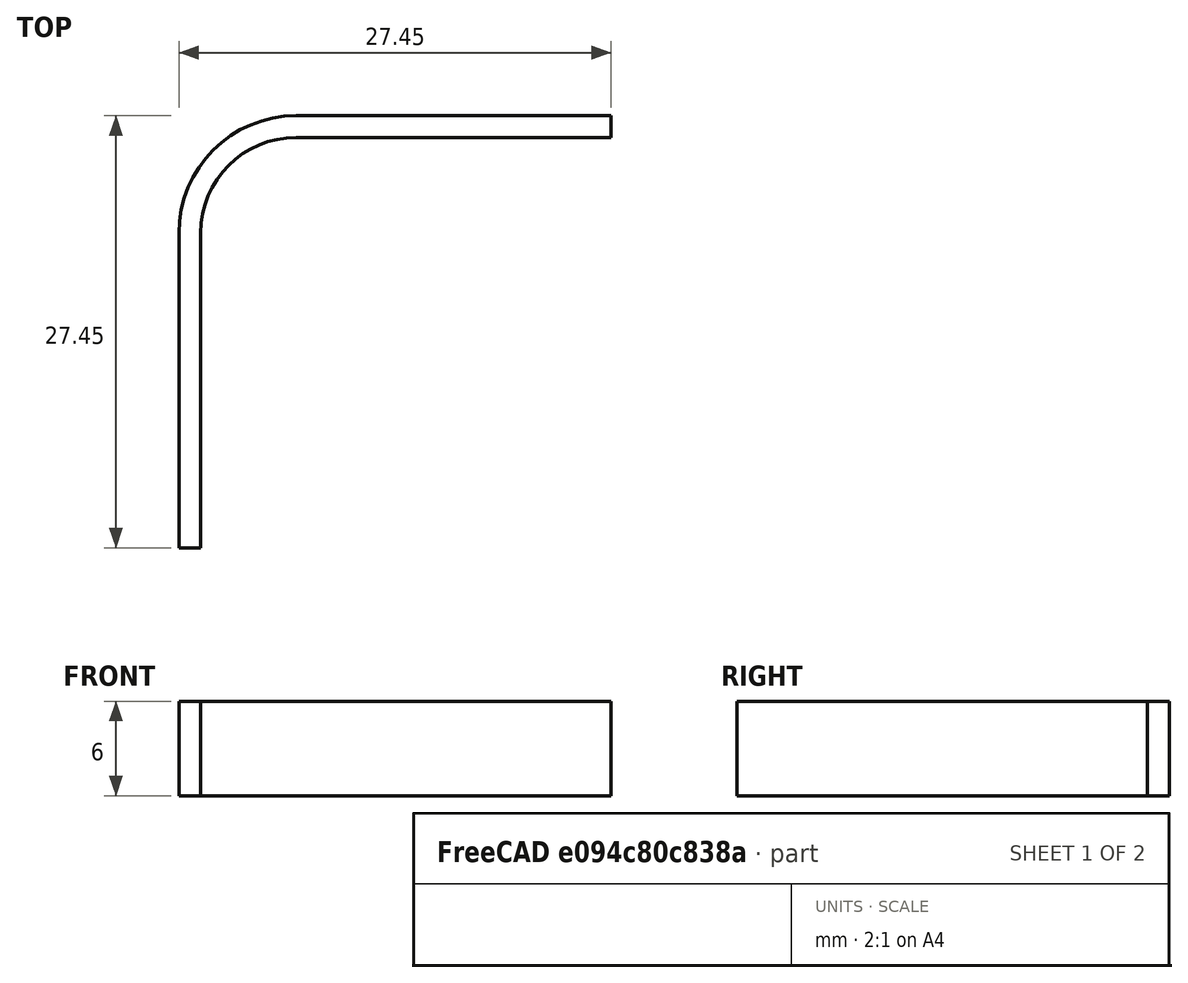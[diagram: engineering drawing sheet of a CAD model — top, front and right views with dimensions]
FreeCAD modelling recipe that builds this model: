
FCSTD DOCUMENT  (FreeCAD 0.20R27078 (Git))
Label: belt 20 idler 90 deg
License: All rights reserved
LicenseURL: http://en.wikipedia.org/wiki/All_rights_reserved
objects: Sketcher::SketchObject×2, PartDesign::AdditivePipe×1, PartDesign::Body×1
note: 5 computed .brp shape members not serialized (recipe doc carries the construction recipe); baked Part::Feature solids carry a one-line shape summary decoded from their .brp

FEATURE [Sketcher::SketchObject] Sketch001
  FullyConstrained = true
  MapMode = 5
  Placement = pos=(0,0,0) rot=(1,0,0;1.5708rad)
  Support = -> [XZ_Plane001]
  sketch-geometry (4):
    g0: LineSegment StartX=0 StartY=6 StartZ=0 EndX=1.38 EndY=6 EndZ=0
    g1: LineSegment StartX=1.38 StartY=6 StartZ=0 EndX=1.38 EndY=0 EndZ=0
    g2: LineSegment StartX=1.38 StartY=0 StartZ=0 EndX=0 EndY=0 EndZ=0
    g3: LineSegment StartX=0 StartY=0 StartZ=0 EndX=0 EndY=6 EndZ=0
  constraints (12):
    c: Coincident(g0,g1)
    c: Coincident(g1,g2)
    c: Coincident(g2,g3)
    c: Coincident(g3,g0)
    c: Horizontal(g0)
    c: Horizontal(g2)
    c: Vertical(g1)
    c: Vertical(g3)
    c: PointOnObject(g0,g-2)
    c: PointOnObject(g1,g-1)
    c: DistanceY(g3,g3) = 6
    c: DistanceX(g0,g0) = 1.38
FEATURE [Sketcher::SketchObject] Sketch002
  ExternalGeometry = -> [Sketch001]
  FullyConstrained = true
  MapMode = 5
  Support = -> [XY_Plane001]
  sketch-geometry (3):
    g0: ArcOfCircle CenterX=7.45 CenterY=2e-16 CenterZ=0 NormalX=0 NormalY=0 NormalZ=1 AngleXU=0 Radius=6.07 StartAngle=1.5708 EndAngle=3.14159
    g1: LineSegment StartX=1.38 StartY=2e-16 StartZ=0 EndX=1.38 EndY=-20 EndZ=0
    g2: LineSegment StartX=7.45 StartY=6.07 StartZ=0 EndX=27.45 EndY=6.07 EndZ=0
  constraints (10):
    c: Coincident(g0,g-3)
    c: Horizontal(g0,g0)
    c: Vertical(g0,g0)
    c: Radius(g0) = 6.07
    c: Coincident(g1,g0)
    c: Vertical(g1)
    c: DistanceY(g1,g1) = 20
    c: Coincident(g2,g0)
    c: Horizontal(g2)
    c: Equal(g1,g2)
FEATURE [PartDesign::AdditivePipe] AdditivePipe
  AuxilleryCurvelinear = true
  AuxillerySpineTangent = false
  Binormal = (0,0,0)
  Mode = 0
  Placement = pos=(0,0,0) rot=(1,0,0;1.5708rad)
  Profile = -> Sketch001
  Spine = -> Sketch002
  SpineTangent = false
  Transformation = 0
  Transition = 0
FEATURE [PartDesign::Body] Body001  label="belt 20 idler 90 deg"
  Group = -> [Sketch001,Sketch002,AdditivePipe]
  Origin = -> Origin001
  Tip = -> AdditivePipe
